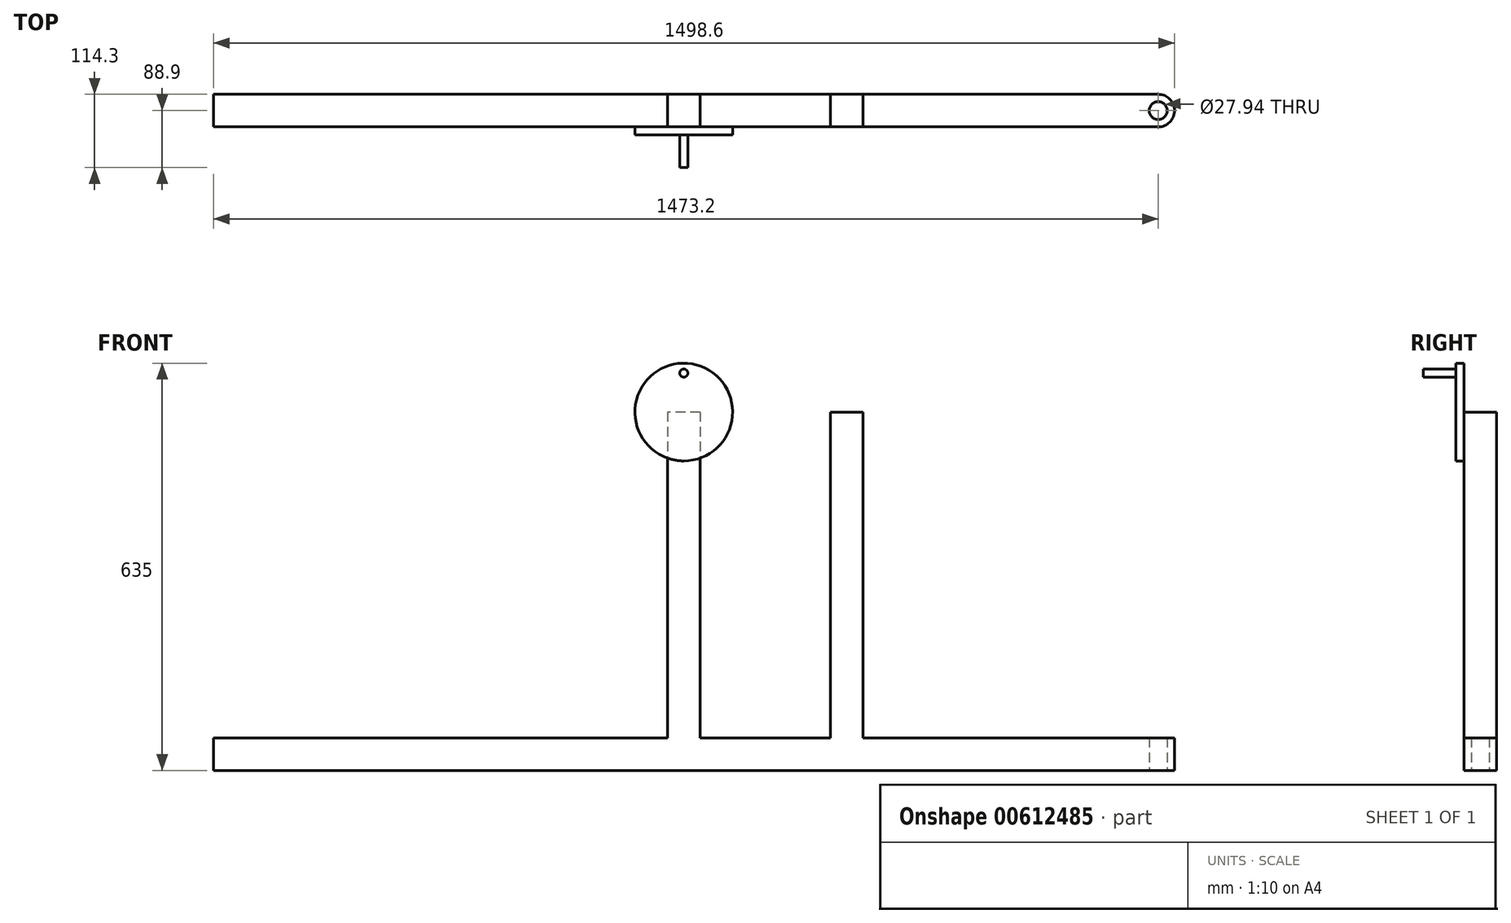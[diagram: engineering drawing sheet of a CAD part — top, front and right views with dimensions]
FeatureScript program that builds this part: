
annotation { "Feature Type Name" : "Feature", "Feature Type Description" : "" }
export const myFeature = defineFeature(function(context is Context, id is Id, definition is map)
    precondition{}
    {
        {
            var Q0;
            Q0=qCreatedBy(makeId("Top.planeOp"),FACE);
            var sketch = newSketch(context, id + "F0", { "sketchPlane" : qUnion([Q0])});
            skLineSegment(sketch, "E0.bottom", {"start": v(739.9, 25.4) * mm, "end": v(-733.3, 25.4) * mm});
            skLineSegment(sketch, "E0.top", {"start": v(739.9, -25.4) * mm, "end": v(-733.3, -25.4) * mm});
            skLineSegment(sketch, "E0.right", {"start": v(-733.3, 25.4) * mm, "end": v(-733.3, -25.4) * mm});
            skPoint(sketch, "E0.middle", {"position": v(3.3, 0) * mm});
            skArc(sketch, "E1", {"start": v(739.9, -25.4) * mm, "mid": v(765.3, 0) * mm, "end": v(739.9, 25.4) * mm});
            skCircle(sketch, "E2", {"center": v(739.9, 0) * mm, "radius": 13.97 * mm});
            skSolve(sketch);
        }
        {
            var Q0;
            Q0 = qSketchRegion(id + "F0", true);
            extrude(context, id + "F1", {"entities" : qUnion([Q0]), "endBound" : BoundingType.SYMMETRIC, "depth" : 50.8 * mm, "offsetDistance" : 25.4 * mm});
        }
        {
            var Q0;
            Q0=makeQuery(id+"F1.opExtrude","CAP_FACE",FACE,{"disambiguationData":[OSD([sQuery(id+"F0.wireOp",EDGE,"E0.bottom"),sQuery(id+"F0.wireOp",EDGE,"E0.top"),sQuery(id+"F0.wireOp",EDGE,"E0.right"),sQuery(id+"F0.wireOp",EDGE,"E1"),sQuery(id+"F0.wireOp",EDGE,"E2")])],"isStart":false});
            var sketch = newSketch(context, id + "F2", { "sketchPlane" : qUnion([Q0])});
            skLineSegment(sketch, "E3.bottom", {"start": v(25.4, 25.4) * mm, "end": v(-25.4, 25.4) * mm});
            skLineSegment(sketch, "E3.top", {"start": v(25.4, -25.4) * mm, "end": v(-25.4, -25.4) * mm});
            skLineSegment(sketch, "E3.left", {"start": v(25.4, 25.4) * mm, "end": v(25.4, -25.4) * mm});
            skLineSegment(sketch, "E3.right", {"start": v(-25.4, 25.4) * mm, "end": v(-25.4, -25.4) * mm});
            skPoint(sketch, "E3.middle", {"position": v(0, 0) * mm});
            skLineSegment(sketch, "E4.bottom", {"start": v(279.4, -25.4) * mm, "end": v(228.6, -25.4) * mm});
            skLineSegment(sketch, "E4.top", {"start": v(279.4, 25.4) * mm, "end": v(228.6, 25.4) * mm});
            skLineSegment(sketch, "E4.left", {"start": v(279.4, -25.4) * mm, "end": v(279.4, 25.4) * mm});
            skLineSegment(sketch, "E4.right", {"start": v(228.6, -25.4) * mm, "end": v(228.6, 25.4) * mm});
            skPoint(sketch, "E4.middle", {"position": v(254, 0) * mm});
            skSolve(sketch);
        }
        {
            var Q0;
            Q0 = qSketchRegion(id + "F2", true);
            extrude(context, id + "F3", {"entities" : qUnion([Q0]), "operationType" : NewBodyOperationType.ADD, "depth" : 508 * mm, "offsetDistance" : 25.4 * mm});
        }
        {
            var Q0;
            Q0=makeQuery(id+"F3.boolean.opBoolean","MERGE",FACE,{"derivedFrom":[makeQuery(id+"F1.opExtrude","SWEPT_FACE",FACE,{"disambiguationData":[OSD([sQuery(id+"F0.wireOp",EDGE,"E0.top")])]}),makeQuery(id+"F3.opExtrude","SWEPT_FACE",FACE,{"disambiguationData":[OSD([sQuery(id+"F2.wireOp",EDGE,"E3.top")])]})]});
            var sketch = newSketch(context, id + "F4", { "sketchPlane" : qUnion([Q0])});
            skCircle(sketch, "E5", {"center": v(0, 533.4) * mm, "radius": 76.2 * mm});
            skSolve(sketch);
        }
        {
            var Q0;
            Q0 = qSketchRegion(id + "F4", true);
            extrude(context, id + "F5", {"entities" : qUnion([Q0]), "operationType" : NewBodyOperationType.ADD, "depth" : 12.7 * mm, "offsetDistance" : 25.4 * mm});
        }
        {
            var Q0;
            Q0=makeQuery(id+"F5.opExtrude","CAP_FACE",FACE,{"disambiguationData":[OSD([sQuery(id+"F4.wireOp",EDGE,"E5")])],"isStart":false});
            var sketch = newSketch(context, id + "F6", { "sketchPlane" : qUnion([Q0])});
            skCircle(sketch, "E6", {"center": v(0, 594.21) * mm, "radius": 6.35 * mm});
            skSolve(sketch);
        }
        {
            var Q0;
            Q0 = qSketchRegion(id + "F6", true);
            extrude(context, id + "F7", {"entities" : qUnion([Q0]), "operationType" : NewBodyOperationType.ADD, "depth" : 50.8 * mm, "offsetDistance" : 25.4 * mm});
        }
    });
